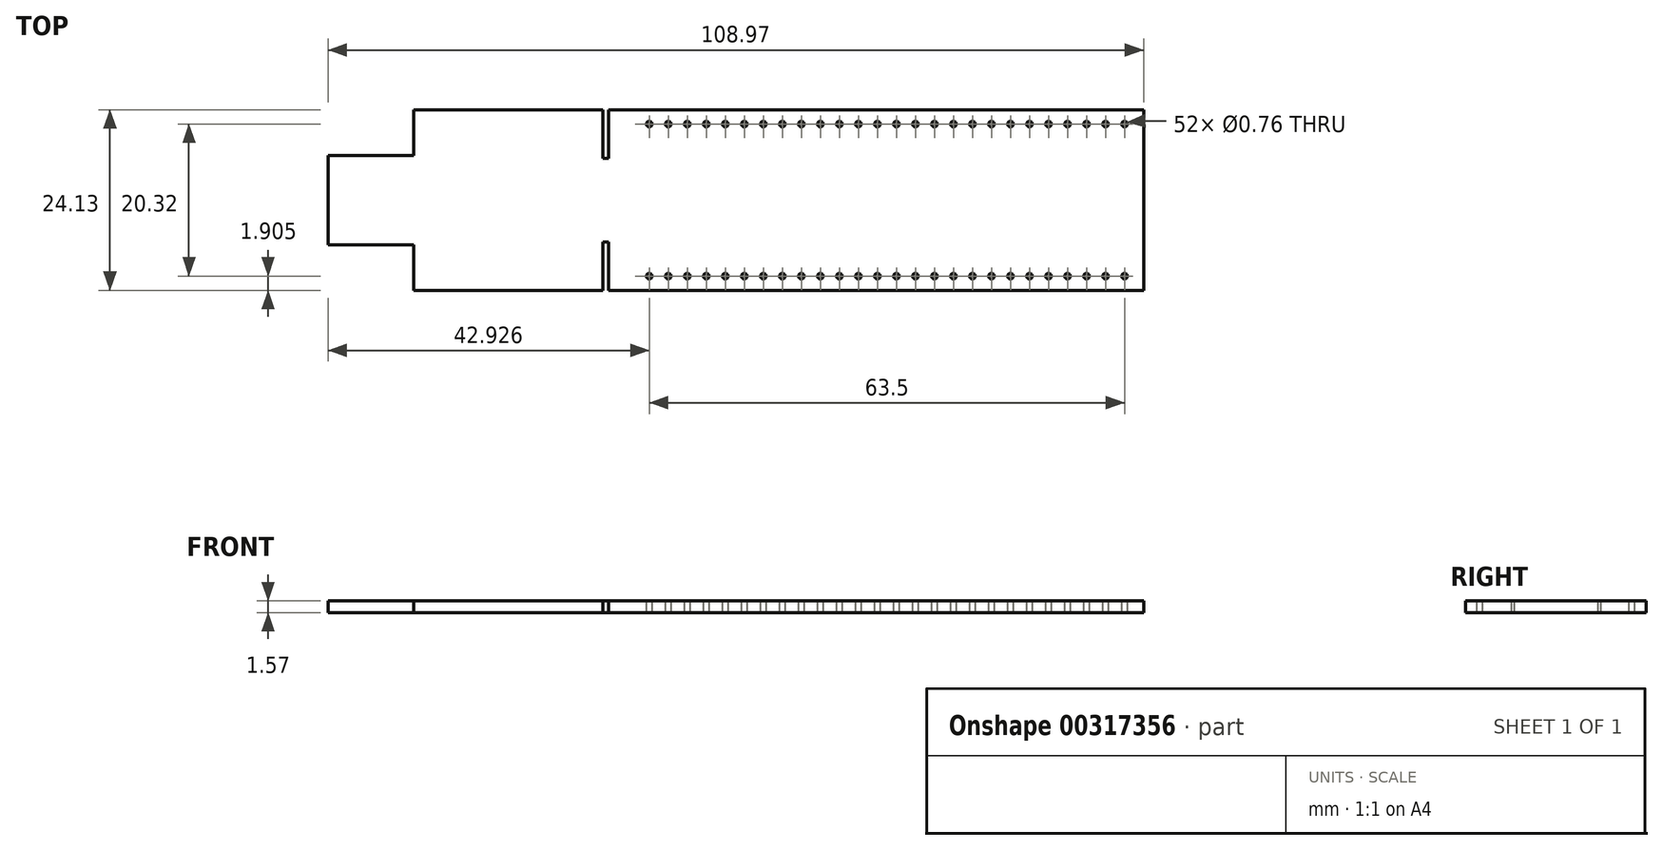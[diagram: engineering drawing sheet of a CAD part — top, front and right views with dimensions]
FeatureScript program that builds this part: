
annotation { "Feature Type Name" : "Feature", "Feature Type Description" : "" }
export const myFeature = defineFeature(function(context is Context, id is Id, definition is map)
    precondition{}
    {
        {
            var Q0;
            Q0=qCreatedBy(makeId("Top.planeOp"),FACE);
            var sketch = newSketch(context, id + "F0", { "sketchPlane" : qUnion([Q0])});
            skLineSegment(sketch, "E0.bottom", {"start": v(0, 0) * mm, "end": v(25.32, 0) * mm});
            skLineSegment(sketch, "E0.top", {"start": v(0, 24.13) * mm, "end": v(25.32, 24.13) * mm});
            skLineSegment(sketch, "E0.left", {"start": v(0, 0) * mm, "end": v(0, 6.1) * mm});
            skLineSegment(sketch, "E0.right", {"start": v(97.54, 0) * mm, "end": v(97.54, 24.13) * mm});
            skLineSegment(sketch, "E1.bottom", {"start": v(0, 18.03) * mm, "end": v(-11.43, 18.03) * mm});
            skLineSegment(sketch, "E1.top", {"start": v(0, 6.1) * mm, "end": v(-11.43, 6.1) * mm});
            skLineSegment(sketch, "E1.right", {"start": v(-11.43, 18.03) * mm, "end": v(-11.43, 6.1) * mm});
            skLineSegment(sketch, "E2.top", {"start": v(25.32, 17.65) * mm, "end": v(26.09, 17.65) * mm});
            skLineSegment(sketch, "E2.left", {"start": v(25.32, 24.13) * mm, "end": v(25.32, 17.65) * mm});
            skLineSegment(sketch, "E2.right", {"start": v(26.09, 24.13) * mm, "end": v(26.09, 17.65) * mm});
            skLineSegment(sketch, "E3.top", {"start": v(25.32, 6.48) * mm, "end": v(26.09, 6.48) * mm});
            skLineSegment(sketch, "E3.left", {"start": v(25.32, 0) * mm, "end": v(25.32, 6.48) * mm});
            skLineSegment(sketch, "E3.right", {"start": v(26.09, 0) * mm, "end": v(26.09, 6.48) * mm});
            skLineSegment(sketch, "E4.trimOffspring", {"start": v(26.09, 24.13) * mm, "end": v(97.54, 24.13) * mm});
            skLineSegment(sketch, "E5.trimOffspring", {"start": v(0, 18.03) * mm, "end": v(0, 24.13) * mm});
            skLineSegment(sketch, "E6.trimOffspring", {"start": v(26.09, 0) * mm, "end": v(97.54, 0) * mm});
            skSolve(sketch);
        }
        {
            var Q0;
            Q0=makeQuery(id+"F0.imprint","IMPRINT",FACE,{"disambiguationData":[TD([[makeQuery(id+"F0.imprint","IMPRINT",EDGE,{"derivedFrom":sQuery(id+"F0.wireOp",EDGE,"E0.bottom")}),1.0]])]});
            extrude(context, id + "F1", {"entities" : qUnion([Q0]), "depth" : 1.57 * mm});
        }
        {
            var Q0;
            Q0=makeQuery(id+"F1.opExtrude","CAP_FACE",FACE,{"disambiguationData":[OSD([sQuery(id+"F0.wireOp",EDGE,"E0.bottom"),sQuery(id+"F0.wireOp",EDGE,"E0.top"),sQuery(id+"F0.wireOp",EDGE,"E0.left"),sQuery(id+"F0.wireOp",EDGE,"E0.right"),sQuery(id+"F0.wireOp",EDGE,"E1.bottom"),sQuery(id+"F0.wireOp",EDGE,"E1.top"),sQuery(id+"F0.wireOp",EDGE,"E1.right"),sQuery(id+"F0.wireOp",EDGE,"E2.top"),sQuery(id+"F0.wireOp",EDGE,"E2.left"),sQuery(id+"F0.wireOp",EDGE,"E2.right"),sQuery(id+"F0.wireOp",EDGE,"E3.top"),sQuery(id+"F0.wireOp",EDGE,"E3.left"),sQuery(id+"F0.wireOp",EDGE,"E3.right"),sQuery(id+"F0.wireOp",EDGE,"E4.trimOffspring"),sQuery(id+"F0.wireOp",EDGE,"E5.trimOffspring"),sQuery(id+"F0.wireOp",EDGE,"E6.trimOffspring")])],"isStart":false});
            var sketch = newSketch(context, id + "F2", { "sketchPlane" : qUnion([Q0])});
            skCircle(sketch, "E7", {"center": v(31.5, 1.9) * mm, "radius": 0.38 * mm});
            skCircle(sketch, "E8.0.1.0", {"center": v(31.5, 22.23) * mm, "radius": 0.38 * mm});
            skCircle(sketch, "E8.1.0.0", {"center": v(34.04, 1.9) * mm, "radius": 0.38 * mm});
            skCircle(sketch, "E8.1.1.0", {"center": v(34.04, 22.23) * mm, "radius": 0.38 * mm});
            skCircle(sketch, "E8.2.0.0", {"center": v(36.58, 1.9) * mm, "radius": 0.38 * mm});
            skCircle(sketch, "E8.2.1.0", {"center": v(36.58, 22.23) * mm, "radius": 0.38 * mm});
            skCircle(sketch, "E8.3.0.0", {"center": v(39.12, 1.9) * mm, "radius": 0.38 * mm});
            skCircle(sketch, "E8.3.1.0", {"center": v(39.12, 22.23) * mm, "radius": 0.38 * mm});
            skCircle(sketch, "E8.4.0.0", {"center": v(41.66, 1.9) * mm, "radius": 0.38 * mm});
            skCircle(sketch, "E8.4.1.0", {"center": v(41.66, 22.23) * mm, "radius": 0.38 * mm});
            skCircle(sketch, "E8.5.0.0", {"center": v(44.2, 1.9) * mm, "radius": 0.38 * mm});
            skCircle(sketch, "E8.5.1.0", {"center": v(44.2, 22.23) * mm, "radius": 0.38 * mm});
            skCircle(sketch, "E8.6.0.0", {"center": v(46.74, 1.9) * mm, "radius": 0.38 * mm});
            skCircle(sketch, "E8.6.1.0", {"center": v(46.74, 22.23) * mm, "radius": 0.38 * mm});
            skCircle(sketch, "E8.7.0.0", {"center": v(49.28, 1.9) * mm, "radius": 0.38 * mm});
            skCircle(sketch, "E8.7.1.0", {"center": v(49.28, 22.23) * mm, "radius": 0.38 * mm});
            skCircle(sketch, "E8.8.0.0", {"center": v(51.82, 1.9) * mm, "radius": 0.38 * mm});
            skCircle(sketch, "E8.8.1.0", {"center": v(51.82, 22.23) * mm, "radius": 0.38 * mm});
            skCircle(sketch, "E8.9.0.0", {"center": v(54.36, 1.9) * mm, "radius": 0.38 * mm});
            skCircle(sketch, "E8.9.1.0", {"center": v(54.36, 22.23) * mm, "radius": 0.38 * mm});
            skCircle(sketch, "E8.10.0.0", {"center": v(56.9, 1.9) * mm, "radius": 0.38 * mm});
            skCircle(sketch, "E8.10.1.0", {"center": v(56.9, 22.23) * mm, "radius": 0.38 * mm});
            skCircle(sketch, "E8.11.0.0", {"center": v(59.44, 1.9) * mm, "radius": 0.38 * mm});
            skCircle(sketch, "E8.11.1.0", {"center": v(59.44, 22.23) * mm, "radius": 0.38 * mm});
            skCircle(sketch, "E8.12.0.0", {"center": v(61.98, 1.9) * mm, "radius": 0.38 * mm});
            skCircle(sketch, "E8.12.1.0", {"center": v(61.98, 22.23) * mm, "radius": 0.38 * mm});
            skCircle(sketch, "E8.13.0.0", {"center": v(64.52, 1.9) * mm, "radius": 0.38 * mm});
            skCircle(sketch, "E8.13.1.0", {"center": v(64.52, 22.23) * mm, "radius": 0.38 * mm});
            skCircle(sketch, "E8.14.0.0", {"center": v(67.06, 1.9) * mm, "radius": 0.38 * mm});
            skCircle(sketch, "E8.14.1.0", {"center": v(67.06, 22.23) * mm, "radius": 0.38 * mm});
            skCircle(sketch, "E8.15.0.0", {"center": v(69.6, 1.9) * mm, "radius": 0.38 * mm});
            skCircle(sketch, "E8.15.1.0", {"center": v(69.6, 22.23) * mm, "radius": 0.38 * mm});
            skCircle(sketch, "E8.16.0.0", {"center": v(72.14, 1.9) * mm, "radius": 0.38 * mm});
            skCircle(sketch, "E8.16.1.0", {"center": v(72.14, 22.23) * mm, "radius": 0.38 * mm});
            skCircle(sketch, "E8.17.0.0", {"center": v(74.68, 1.9) * mm, "radius": 0.38 * mm});
            skCircle(sketch, "E8.17.1.0", {"center": v(74.68, 22.23) * mm, "radius": 0.38 * mm});
            skCircle(sketch, "E8.18.0.0", {"center": v(77.22, 1.9) * mm, "radius": 0.38 * mm});
            skCircle(sketch, "E8.18.1.0", {"center": v(77.22, 22.23) * mm, "radius": 0.38 * mm});
            skCircle(sketch, "E8.19.0.0", {"center": v(79.76, 1.9) * mm, "radius": 0.38 * mm});
            skCircle(sketch, "E8.19.1.0", {"center": v(79.76, 22.23) * mm, "radius": 0.38 * mm});
            skCircle(sketch, "E8.20.0.0", {"center": v(82.3, 1.9) * mm, "radius": 0.38 * mm});
            skCircle(sketch, "E8.20.1.0", {"center": v(82.3, 22.23) * mm, "radius": 0.38 * mm});
            skCircle(sketch, "E8.21.0.0", {"center": v(84.84, 1.9) * mm, "radius": 0.38 * mm});
            skCircle(sketch, "E8.21.1.0", {"center": v(84.84, 22.23) * mm, "radius": 0.38 * mm});
            skCircle(sketch, "E8.22.0.0", {"center": v(87.38, 1.9) * mm, "radius": 0.38 * mm});
            skCircle(sketch, "E8.22.1.0", {"center": v(87.38, 22.23) * mm, "radius": 0.38 * mm});
            skCircle(sketch, "E8.23.0.0", {"center": v(89.92, 1.9) * mm, "radius": 0.38 * mm});
            skCircle(sketch, "E8.23.1.0", {"center": v(89.92, 22.23) * mm, "radius": 0.38 * mm});
            skCircle(sketch, "E8.24.0.0", {"center": v(92.46, 1.9) * mm, "radius": 0.38 * mm});
            skCircle(sketch, "E8.24.1.0", {"center": v(92.46, 22.23) * mm, "radius": 0.38 * mm});
            skCircle(sketch, "E8.25.0.0", {"center": v(95, 1.9) * mm, "radius": 0.38 * mm});
            skCircle(sketch, "E8.25.1.0", {"center": v(95, 22.23) * mm, "radius": 0.38 * mm});
            skLineSegment(sketch, "E8.direction1", {"start": v(31.5, 1.9) * mm, "end": v(34.04, 1.9) * mm, "construction": true});
            skLineSegment(sketch, "E8.direction2", {"start": v(31.5, 1.9) * mm, "end": v(31.5, 22.23) * mm, "construction": true});
            skSolve(sketch);
        }
        {
            var Q0;
            Q0 = qSketchRegion(id + "F2", true);
            extrude(context, id + "F3", {"entities" : qUnion([Q0]), "operationType" : NewBodyOperationType.REMOVE, "endBound" : BoundingType.THROUGH_ALL, "oppositeDirection" : true, "depth" : 25.4 * mm});
        }
    });
